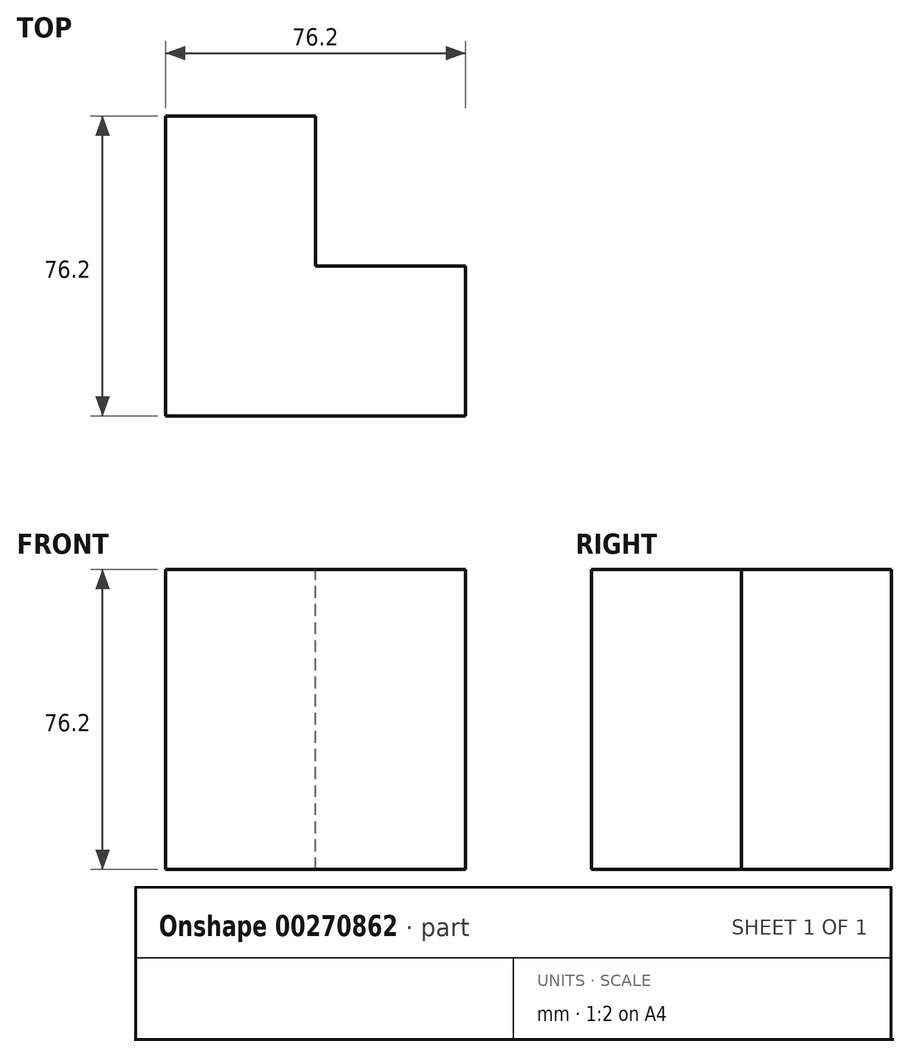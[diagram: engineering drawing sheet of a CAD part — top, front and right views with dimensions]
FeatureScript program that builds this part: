
annotation { "Feature Type Name" : "Feature", "Feature Type Description" : "" }
export const myFeature = defineFeature(function(context is Context, id is Id, definition is map)
    precondition{}
    {
        {
            var Q0;
            Q0=qCreatedBy(makeId("Front.planeOp"),FACE);
            var sketch = newSketch(context, id + "F0", { "sketchPlane" : qUnion([Q0])});
            skLineSegment(sketch, "E0.bottom", {"start": v(0, 0) * mm, "end": v(-76.2, 0) * mm});
            skLineSegment(sketch, "E0.top", {"start": v(0, 76.2) * mm, "end": v(-76.2, 76.2) * mm});
            skLineSegment(sketch, "E0.left", {"start": v(0, 0) * mm, "end": v(0, 76.2) * mm});
            skLineSegment(sketch, "E0.right", {"start": v(-76.2, 0) * mm, "end": v(-76.2, 76.2) * mm});
            skLineSegment(sketch, "E1.bottom", {"start": v(0, 76.2) * mm, "end": v(-38.1, 76.2) * mm});
            skLineSegment(sketch, "E1.left", {"start": v(0, 76.2) * mm, "end": v(0, 38.1) * mm});
            skSolve(sketch);
        }
        {
            var Q0;
            Q0 = qSketchRegion(id + "F0", true);
            extrude(context, id + "F1", {"entities" : qUnion([Q0]), "depth" : 76.2 * mm});
        }
        {
            var Q0;
            Q0=makeQuery(id+"F1.opExtrude","SWEPT_FACE",FACE,{"disambiguationData":[OSD([sQuery(id+"F0.wireOp",EDGE,"E0.top"),sQuery(id+"F0.wireOp",EDGE,"E1.bottom")])]});
            var sketch = newSketch(context, id + "F2", { "sketchPlane" : qUnion([Q0])});
            skLineSegment(sketch, "E2.bottom", {"start": v(0, 0) * mm, "end": v(-38.1, 0) * mm});
            skLineSegment(sketch, "E2.top", {"start": v(0, -38.1) * mm, "end": v(-38.1, -38.1) * mm});
            skLineSegment(sketch, "E2.left", {"start": v(0, 0) * mm, "end": v(0, -38.1) * mm});
            skLineSegment(sketch, "E2.right", {"start": v(-38.1, 0) * mm, "end": v(-38.1, -38.1) * mm});
            skSolve(sketch);
        }
        {
            var Q0;
            Q0 = qSketchRegion(id + "F2", true);
            extrude(context, id + "F3", {"entities" : qUnion([Q0]), "operationType" : NewBodyOperationType.REMOVE, "oppositeDirection" : true, "depth" : 76.2 * mm});
        }
    });
